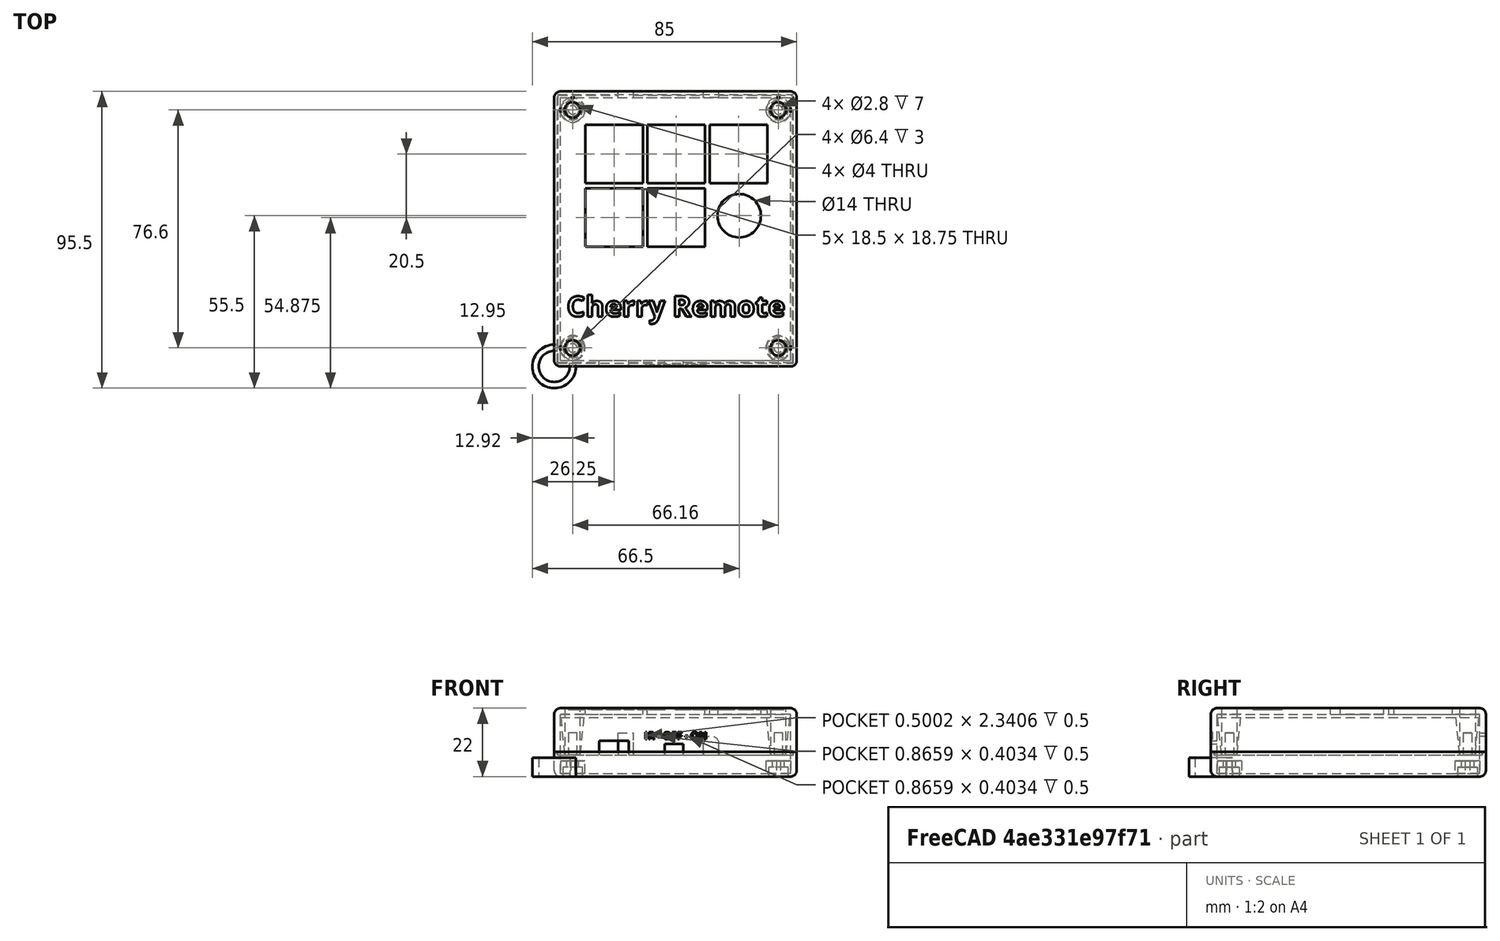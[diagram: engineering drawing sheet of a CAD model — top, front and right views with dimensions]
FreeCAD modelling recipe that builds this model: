
FCSTD DOCUMENT  (FreeCAD 0.20R29603 (Git))
Label: cherry_remote_new
License: All rights reserved
LicenseURL: http://en.wikipedia.org/wiki/All_rights_reserved
objects: Part::Cylinder×24, Part::Box×17, Part::Cut×11, Part::MultiFuse×9, Part::Cone×4, Part::Part2DObjectPython×2, Part::Extrusion×2, Part::Fillet×2
note: 71 computed .brp shape members not serialized (recipe doc carries the construction recipe); baked Part::Feature solids carry a one-line shape summary decoded from their .brp

FEATURE [Part::Box] Box  label="Cube(inner_base)"
  AttacherType = Attacher::AttachEngine3D
  Height = 8
  Length = 74
  Width = 84.5
FEATURE [Part::Cylinder] Cylinder  label="Cylinder(bottom_right_mount)"
  Angle = 360
  AttacherType = Attacher::AttachEngine3D
  FirstAngle = 0
  Height = 4
  Placement = pos=(70.08,3.95,0) rot=(0,0,1;0rad)
  Radius = 4
  SecondAngle = 0
FEATURE [Part::Cylinder] Cylinder001  label="Cylinder001(bottom_left_mount)"
  Angle = 360
  AttacherType = Attacher::AttachEngine3D
  FirstAngle = 0
  Height = 4
  Placement = pos=(3.92,3.95,0) rot=(0,0,1;0rad)
  Radius = 4
  SecondAngle = 0
FEATURE [Part::Cylinder] Cylinder002  label="Cylinder(top_right_mount)"
  Angle = 360
  AttacherType = Attacher::AttachEngine3D
  FirstAngle = 0
  Height = 4
  Placement = pos=(70.08,80.55,0) rot=(0,0,1;0rad)
  Radius = 4
  SecondAngle = 0
FEATURE [Part::Cylinder] Cylinder003  label="Cylinder001(top_left_mount)"
  Angle = 360
  AttacherType = Attacher::AttachEngine3D
  FirstAngle = 0
  Height = 4
  Placement = pos=(3.92,80.55,0) rot=(0,0,1;0rad)
  Radius = 4
  SecondAngle = 0
FEATURE [Part::Box] Box001  label="Cube(outer_base)"
  AttacherType = Attacher::AttachEngine3D
  Height = 8
  Length = 78
  Placement = pos=(-2,-2,-1) rot=(0,0,1;0rad)
  Width = 88.5
FEATURE [Part::Box] Box002  label="Cube(outer_lid)"
  AttacherType = Attacher::AttachEngine3D
  Height = 14
  Length = 78
  Placement = pos=(-2,-2,7) rot=(0,0,1;0rad)
  Width = 88.5
FEATURE [Part::Box] Box003  label="Cube(inner_lid)"
  AttacherType = Attacher::AttachEngine3D
  Height = 13
  Length = 74
  Placement = pos=(0,0,6) rot=(0,0,1;0rad)
  Width = 84.5
FEATURE [Part::Box] Box004  label="Cube(ir_receiver)"
  AttacherType = Attacher::AttachEngine3D
  Height = 7
  Length = 5
  Placement = pos=(18.5,84.5,6) rot=(0,0,1;0rad)
  Width = 2
FEATURE [Part::Box] Box005  label="Cube(ir_blaster)"
  AttacherType = Attacher::AttachEngine3D
  Height = 3.5
  Length = 5
  Placement = pos=(46,84.5,6) rot=(0,0,1;0rad)
  Width = 2
FEATURE [Part::Cylinder] Cylinder004  label="Cylinder(ir_blaster)"
  Angle = 360
  AttacherType = Attacher::AttachEngine3D
  FirstAngle = 0
  Height = 2
  Placement = pos=(48.5,86.5,9.5) rot=(1,0,0;1.5708rad)
  Radius = 2.5
  SecondAngle = 0
FEATURE [Part::Box] Box006  label="Cube(usb_c)"
  AttacherType = Attacher::AttachEngine3D
  Height = 4.5
  Length = 9.5
  Placement = pos=(12.5,-2,6) rot=(0,0,1;0rad)
  Width = 2
FEATURE [Part::Box] Box007  label="Cube(switch_hole)"
  AttacherType = Attacher::AttachEngine3D
  Height = 3.5
  Length = 6
  Placement = pos=(33.5,-2,6) rot=(0,0,1;0rad)
  Width = 2
FEATURE [Part::Box] Box008  label="Cube(button_top_left)"
  AttacherType = Attacher::AttachEngine3D
  Height = 2
  Length = 18.5
  Placement = pos=(8,57,19) rot=(0,0,1;0rad)
  Width = 18.75
FEATURE [Part::Box] Box009  label="Cube(button_top_mid)"
  AttacherType = Attacher::AttachEngine3D
  Height = 2
  Length = 18.5
  Placement = pos=(28,57,19) rot=(0,0,1;0rad)
  Width = 18.75
FEATURE [Part::Box] Box010  label="Cube(button_top_right)"
  AttacherType = Attacher::AttachEngine3D
  Height = 2
  Length = 18.5
  Placement = pos=(48,57,19) rot=(0,0,1;0rad)
  Width = 18.75
FEATURE [Part::Box] Box011  label="Cube(button_bottom_left)"
  AttacherType = Attacher::AttachEngine3D
  Height = 2
  Length = 18.5
  Placement = pos=(8,36.5,19) rot=(0,0,1;0rad)
  Width = 18.75
FEATURE [Part::Box] Box012  label="Cube(button_bottom_mid)"
  AttacherType = Attacher::AttachEngine3D
  Height = 2
  Length = 18.5
  Placement = pos=(28,36.5,19) rot=(0,0,1;0rad)
  Width = 18.75
FEATURE [Part::Cylinder] Cylinder005  label="Cylinder(jack_hole)"
  Angle = 360
  AttacherType = Attacher::AttachEngine3D
  FirstAngle = 0
  Height = 2
  Placement = pos=(57.5,46.5,19) rot=(0,0,1;0rad)
  Radius = 7
  SecondAngle = 0
FEATURE [Part::Box] Box013  label="Cube(inner_base_lip)"
  AttacherType = Attacher::AttachEngine3D
  Height = 1
  Length = 76
  Placement = pos=(-1,-1,6) rot=(0,0,1;0rad)
  Width = 86.5
FEATURE [Part::Cut] Cut
  Base = -> Box001
  Tool = -> Box
FEATURE [Part::Cut] Cut001
  Base = -> Cut
  Tool = -> Box013
FEATURE [Part::Cylinder] Cylinder006  label="Cylinder(bottom_right_mount_clear)"
  Angle = 360
  AttacherType = Attacher::AttachEngine3D
  FirstAngle = 0
  Height = 2
  Placement = pos=(70.08,3.95,2) rot=(0,0,1;0rad)
  Radius = 2
  SecondAngle = 0
FEATURE [Part::Cylinder] Cylinder007  label="Cylinder001(bottom_left_mount_clear)"
  Angle = 360
  AttacherType = Attacher::AttachEngine3D
  FirstAngle = 0
  Height = 2
  Placement = pos=(3.92,3.95,2) rot=(0,0,1;0rad)
  Radius = 2
  SecondAngle = 0
FEATURE [Part::Cylinder] Cylinder008  label="Cylinder(top_right_mount_clear)"
  Angle = 360
  AttacherType = Attacher::AttachEngine3D
  FirstAngle = 0
  Height = 2
  Placement = pos=(70.08,80.55,2) rot=(0,0,1;0rad)
  Radius = 2
  SecondAngle = 0
FEATURE [Part::Cylinder] Cylinder009  label="Cylinder001(top_left_mount_clear)"
  Angle = 360
  AttacherType = Attacher::AttachEngine3D
  FirstAngle = 0
  Height = 2
  Placement = pos=(3.92,80.55,2) rot=(0,0,1;0rad)
  Radius = 2
  SecondAngle = 0
FEATURE [Part::Cylinder] Cylinder010  label="Cylinder(bottom_right_mount_head_clear)"
  Angle = 360
  AttacherType = Attacher::AttachEngine3D
  FirstAngle = 0
  Height = 3
  Placement = pos=(70.08,3.95,-1) rot=(0,0,1;0rad)
  Radius = 3.2
  SecondAngle = 0
FEATURE [Part::Cylinder] Cylinder011  label="Cylinder001(bottom_left_mount_head_clear)"
  Angle = 360
  AttacherType = Attacher::AttachEngine3D
  FirstAngle = 0
  Height = 3
  Placement = pos=(3.92,3.95,-1) rot=(0,0,1;0rad)
  Radius = 3.2
  SecondAngle = 0
FEATURE [Part::Cylinder] Cylinder012  label="Cylinder(top_right_mount_head_clear)"
  Angle = 360
  AttacherType = Attacher::AttachEngine3D
  FirstAngle = 0
  Height = 3
  Placement = pos=(70.08,80.55,-1) rot=(0,0,1;0rad)
  Radius = 3.2
  SecondAngle = 0
FEATURE [Part::Cylinder] Cylinder013  label="Cylinder001(top_left_mount_head_clear)"
  Angle = 360
  AttacherType = Attacher::AttachEngine3D
  FirstAngle = 0
  Height = 3
  Placement = pos=(3.92,80.55,-1) rot=(0,0,1;0rad)
  Radius = 3.2
  SecondAngle = 0
FEATURE [Part::MultiFuse] Fusion
  Shapes = -> [Cut001,Cylinder001,Cylinder,Cylinder002,Cylinder003]
FEATURE [Part::MultiFuse] Fusion001
  Shapes = -> [Cylinder006,Cylinder007,Cylinder008,Cylinder009,Cylinder010,Cylinder011,Cylinder012,Cylinder013]
FEATURE [Part::Cut] Cut002
  Base = -> Fusion
  Tool = -> Fusion001
FEATURE [Part::Box] Box014  label="Cube"
  AttacherType = Attacher::AttachEngine3D
  Height = 1
  Length = 74
  Placement = pos=(0,0,18) rot=(0,0,1;0rad)
  Width = 84.5
FEATURE [Part::Cylinder] Cylinder014  label="Cylinder001(top_left_standoff)"
  Angle = 360
  AttacherType = Attacher::AttachEngine3D
  FirstAngle = 0
  Height = 15
  Placement = pos=(3.92,80.55,6) rot=(0,0,1;0rad)
  Radius = 2.5
  SecondAngle = 0
FEATURE [Part::Cylinder] Cylinder015  label="Cylinder(bottom_right_standoff)"
  Angle = 360
  AttacherType = Attacher::AttachEngine3D
  FirstAngle = 0
  Height = 15
  Placement = pos=(70.08,3.95,6) rot=(0,0,1;0rad)
  Radius = 2.5
  SecondAngle = 0
FEATURE [Part::Cylinder] Cylinder016  label="Cylinder001(bottom_left_standoff)"
  Angle = 360
  AttacherType = Attacher::AttachEngine3D
  FirstAngle = 0
  Height = 15
  Placement = pos=(3.92,3.95,6) rot=(0,0,1;0rad)
  Radius = 2.5
  SecondAngle = 0
FEATURE [Part::Cylinder] Cylinder017  label="Cylinder(top_right_standoff)"
  Angle = 360
  AttacherType = Attacher::AttachEngine3D
  FirstAngle = 0
  Height = 15
  Placement = pos=(70.08,80.55,6) rot=(0,0,1;0rad)
  Radius = 2.5
  SecondAngle = 0
FEATURE [Part::Box] Box015  label="Cube(inner_lid_lip)"
  AttacherType = Attacher::AttachEngine3D
  Height = 1
  Length = 75.5
  Placement = pos=(-0.75,-0.75,6) rot=(0,0,1;0rad)
  Width = 86
FEATURE [Part::Cylinder] Cylinder018  label="Cylinder001(top_left_thread)"
  Angle = 360
  AttacherType = Attacher::AttachEngine3D
  FirstAngle = 0
  Height = 7
  Placement = pos=(3.92,80.55,6) rot=(0,0,1;0rad)
  Radius = 1.4
  SecondAngle = 0
FEATURE [Part::Cylinder] Cylinder019  label="Cylinder(bottom_right_thread)"
  Angle = 360
  AttacherType = Attacher::AttachEngine3D
  FirstAngle = 0
  Height = 7
  Placement = pos=(70.08,3.95,6) rot=(0,0,1;0rad)
  Radius = 1.4
  SecondAngle = 0
FEATURE [Part::Cylinder] Cylinder020  label="Cylinder001(bottom_left_thread)"
  Angle = 360
  AttacherType = Attacher::AttachEngine3D
  FirstAngle = 0
  Height = 7
  Placement = pos=(3.92,3.95,6) rot=(0,0,1;0rad)
  Radius = 1.4
  SecondAngle = 0
FEATURE [Part::Cylinder] Cylinder021  label="Cylinder(top_right_thread)"
  Angle = 360
  AttacherType = Attacher::AttachEngine3D
  FirstAngle = 0
  Height = 7
  Placement = pos=(70.08,80.55,6) rot=(0,0,1;0rad)
  Radius = 1.4
  SecondAngle = 0
FEATURE [Part::Part2DObjectPython] ShapeString  # Draft 2D object (typed FeaturePython)
  FontFile = <userpath>/stuff/3dprinting/fonts/open-sans/OpenSans-Bold.ttf
  MakeFace = true
  Placement = pos=(2,14,20.5) rot=(0,0,1;0rad)
  Size = 8.5
  String = Cherry Remote
  Tracking = 0
FEATURE [Part::Part2DObjectPython] ShapeString001  # Draft 2D object (typed FeaturePython)
  FontFile = <userpath>/stuff/3dprinting/fonts/open-sans/OpenSans-Bold.ttf
  MakeFace = true
  Placement = pos=(27,-1.5,11) rot=(1,0,0;1.5708rad)
  Size = 3
  String = IR - OFF - ON
  Tracking = 0
FEATURE [Part::Extrusion] Extrude
  Base = -> ShapeString001
  Dir = (0,-1,2e-16)
  DirMode = 2
  FaceMakerClass = Part::FaceMakerBullseye
  LengthFwd = 0.5
  LengthRev = 0
  Solid = false
  Symmetric = false
FEATURE [Part::Extrusion] Extrude001
  Base = -> ShapeString
  Dir = (0,0,1)
  DirMode = 2
  FaceMakerClass = Part::FaceMakerBullseye
  LengthFwd = 0.5
  LengthRev = 0
  Solid = false
  Symmetric = false
FEATURE [Part::Cylinder] Cylinder022  label="Cylinder(loop_inner)"
  Angle = 360
  AttacherType = Attacher::AttachEngine3D
  FirstAngle = 0
  Height = 6
  Placement = pos=(-2,-2,-1) rot=(0,0,1;1.5708rad)
  Radius = 5
  SecondAngle = 0
FEATURE [Part::Cylinder] Cylinder023  label="Cylinder(loop_outer)"
  Angle = 360
  AttacherType = Attacher::AttachEngine3D
  FirstAngle = 0
  Height = 6
  Placement = pos=(-2,-2,-1) rot=(0,0,1;1.5708rad)
  Radius = 7
  SecondAngle = 0
FEATURE [Part::Box] Box016  label="Cube001(loop_cutter)"
  AttacherType = Attacher::AttachEngine3D
  Height = 10
  Length = 10
  Placement = pos=(-1,-1,-1) rot=(0,0,1;0rad)
  Width = 10
FEATURE [Part::Cut] Cut003
  Base = -> Cylinder023
  Tool = -> Cylinder022
FEATURE [Part::Cut] Cut004
  Base = -> Cut003
  Tool = -> Box016
FEATURE [Part::Fillet] Fillet
  Base = -> Cut002
  Edges = 8 edges r=2: [Edge101,Edge102,Edge103,Edge104,Edge105,Edge106,Edge107,Edge108]
FEATURE [Part::MultiFuse] Fusion002
  Shapes = -> [Cut004,Fillet]
FEATURE [Part::MultiFuse] Fusion004
  Shapes = -> [Box005,Box004,Cylinder004,Box006,Box007]
FEATURE [Part::MultiFuse] Fusion006
  Shapes = -> [Cylinder021,Cylinder020,Cylinder019,Cylinder018]
FEATURE [Part::MultiFuse] Fusion008
  Shapes = -> [Box002,Box015]
FEATURE [Part::Cut] Cut007
  Base = -> Fusion008
  Tool = -> Box003
FEATURE [Part::MultiFuse] Fusion009
  Shapes = -> [Box008,Box009,Box010,Box011,Box012,Cylinder005]
FEATURE [Part::Cone] Cone  label="Cone(bottom_left_standoff)"
  Angle = 360
  AttacherType = Attacher::AttachEngine3D
  Height = 15
  Placement = pos=(3.92,3.95,6) rot=(0,0,1;0rad)
  Radius1 = 2.5
  Radius2 = 4
FEATURE [Part::Cone] Cone001  label="Cone(bottom_right_standoff)"
  Angle = 360
  AttacherType = Attacher::AttachEngine3D
  Height = 15
  Placement = pos=(70.08,3.95,6) rot=(0,0,1;0rad)
  Radius1 = 2.5
  Radius2 = 4
FEATURE [Part::Cone] Cone002  label="Cone(top_left_standoff)"
  Angle = 360
  AttacherType = Attacher::AttachEngine3D
  Height = 15
  Placement = pos=(3.92,80.55,6) rot=(0,0,1;0rad)
  Radius1 = 2.5
  Radius2 = 4
FEATURE [Part::Cone] Cone003  label="Cone(top_right_standoff)"
  Angle = 360
  AttacherType = Attacher::AttachEngine3D
  Height = 15
  Placement = pos=(70.08,80.55,6) rot=(0,0,1;0rad)
  Radius1 = 2.5
  Radius2 = 4
FEATURE [Part::MultiFuse] Fusion010
  Shapes = -> [Cone,Cone001,Cone002,Cone003]
FEATURE [Part::Cut] Cut010
  Base = -> Fusion010
  Tool = -> Fusion006
FEATURE [Part::Cut] Cut011
  Base = -> Cut007
  Tool = -> Fusion009
FEATURE [Part::Cut] Cut012
  Base = -> Cut011
  Tool = -> Extrude001
FEATURE [Part::Cut] Cut013
  Base = -> Cut012
  Tool = -> Extrude
FEATURE [Part::Cut] Cut014
  Base = -> Cut013
  Tool = -> Fusion004
FEATURE [Part::Fillet] Fillet001
  Base = -> Cut014
  Edges = 8 edges r=2: [Edge1,Edge2,Edge3,Edge14,Edge15,Edge90,Edge91,Edge310]
FEATURE [Part::MultiFuse] Fusion011
  Shapes = -> [Fillet001,Cut010]
